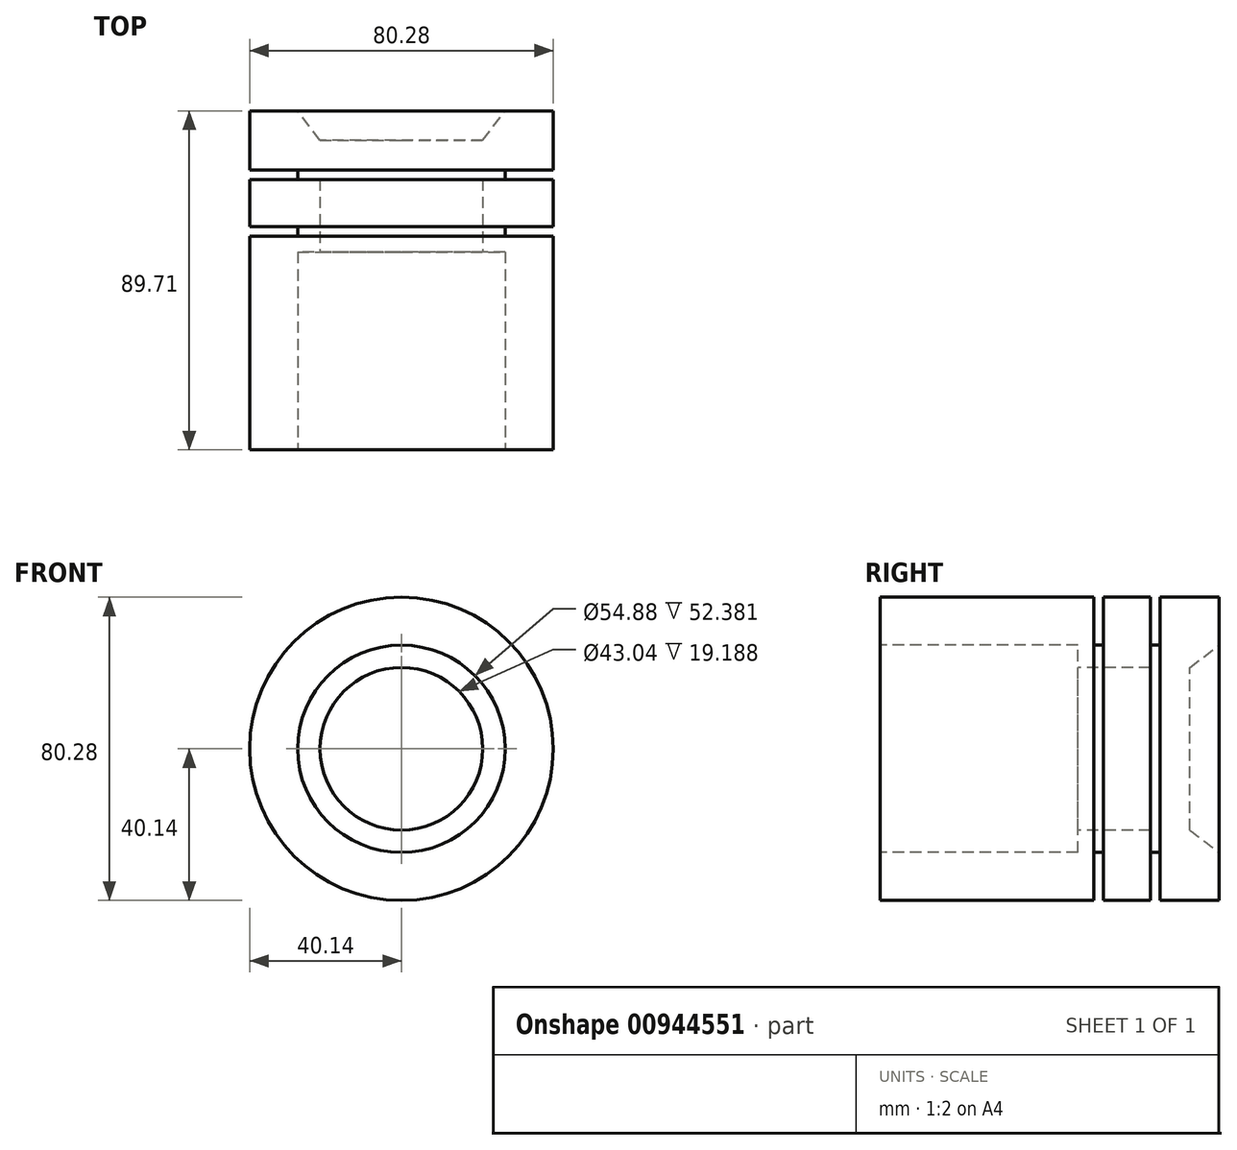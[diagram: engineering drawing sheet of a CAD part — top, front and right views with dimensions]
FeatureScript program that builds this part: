
annotation { "Feature Type Name" : "Feature", "Feature Type Description" : "" }
export const myFeature = defineFeature(function(context is Context, id is Id, definition is map)
    precondition{}
    {
        {
            var Q0;
            Q0=qCreatedBy(makeId("Top.planeOp"),FACE);
            var sketch = newSketch(context, id + "F0", { "sketchPlane" : qUnion([Q0])});
            skLineSegment(sketch, "E0", {"start": v(0, 48.76) * mm, "end": v(-21.52, 48.76) * mm});
            skLineSegment(sketch, "E1", {"start": v(-21.52, 48.76) * mm, "end": v(-27.44, 56.47) * mm});
            skLineSegment(sketch, "E2", {"start": v(-27.44, 56.47) * mm, "end": v(-40.14, 56.47) * mm});
            skLineSegment(sketch, "E3", {"start": v(-40.14, 56.47) * mm, "end": v(-40.14, 40.87) * mm});
            skLineSegment(sketch, "E4", {"start": v(-40.14, 40.87) * mm, "end": v(-27.44, 40.87) * mm});
            skLineSegment(sketch, "E5", {"start": v(-27.44, 40.87) * mm, "end": v(-27.44, 38.33) * mm});
            skLineSegment(sketch, "E6", {"start": v(-27.44, 38.33) * mm, "end": v(-40.14, 38.33) * mm});
            skLineSegment(sketch, "E7", {"start": v(-40.14, 38.33) * mm, "end": v(-40.14, 25.9) * mm});
            skLineSegment(sketch, "E8", {"start": v(-40.14, 25.9) * mm, "end": v(-27.44, 25.9) * mm});
            skLineSegment(sketch, "E9", {"start": v(-27.44, 25.9) * mm, "end": v(-27.44, 23.36) * mm});
            skLineSegment(sketch, "E10", {"start": v(-27.44, 23.36) * mm, "end": v(-40.14, 23.36) * mm});
            skLineSegment(sketch, "E11", {"start": v(-40.14, 23.36) * mm, "end": v(-40.14, -33.24) * mm});
            skLineSegment(sketch, "E12", {"start": v(-40.14, -33.24) * mm, "end": v(-27.44, -33.24) * mm});
            skLineSegment(sketch, "E13", {"start": v(-27.44, -33.24) * mm, "end": v(-27.44, 19.14) * mm});
            skLineSegment(sketch, "E14", {"start": v(-27.44, 19.14) * mm, "end": v(-21.52, 19.14) * mm});
            skLineSegment(sketch, "E15", {"start": v(-21.52, 19.14) * mm, "end": v(-21.52, 38.33) * mm});
            skLineSegment(sketch, "E16", {"start": v(-21.52, 38.33) * mm, "end": v(0, 38.33) * mm});
            skLineSegment(sketch, "E17", {"start": v(0, 38.33) * mm, "end": v(0, 48.76) * mm});
            skSolve(sketch);
        }
        {
            var Q0;
            Q0 = qSketchRegion(id + "F0", true);
            var Q1;
            Q1=sQuery(id+"F0.wireOp",EDGE,"E17");
            revolve(context, id + "F1", {"surfaceOperationType" : NewSurfaceOperationType.NEW, "entities" : qUnion([Q0]), "axis" : qUnion([Q1]), "revolveType" : RevolveType.FULL});
        }
    });
